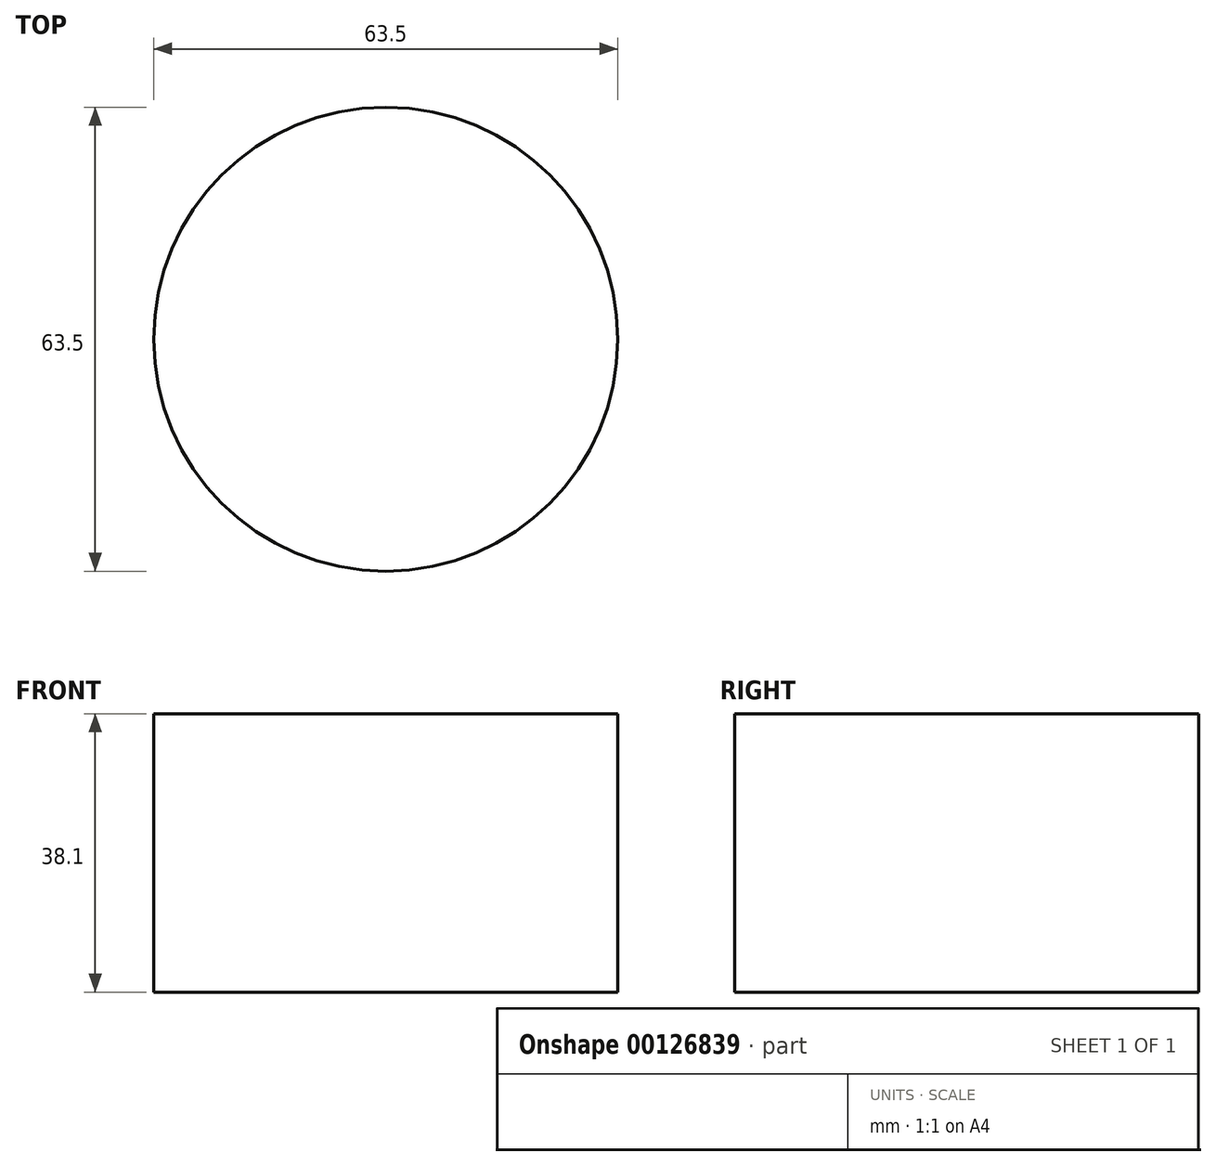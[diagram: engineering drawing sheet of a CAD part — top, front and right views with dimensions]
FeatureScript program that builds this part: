
annotation { "Feature Type Name" : "Feature", "Feature Type Description" : "" }
export const myFeature = defineFeature(function(context is Context, id is Id, definition is map)
    precondition{}
    {
        {
            var Q0;
            Q0=qCreatedBy(makeId("Top.planeOp"),FACE);
            var sketch = newSketch(context, id + "F0", { "sketchPlane" : qUnion([Q0])});
            skCircle(sketch, "E0", {"center": v(0, 0) * mm, "radius": 31.75 * mm});
            skSolve(sketch);
        }
        {
            var Q0;
            Q0=makeQuery(id+"F0.imprint","IMPRINT",FACE,{"disambiguationData":[TD([[makeQuery(id+"F0.imprint","IMPRINT",EDGE,{"derivedFrom":sQuery(id+"F0.wireOp",EDGE,"E0")}),1.0]])]});
            extrude(context, id + "F1", {"entities" : qUnion([Q0]), "depth" : 38.1 * mm});
        }
    });
